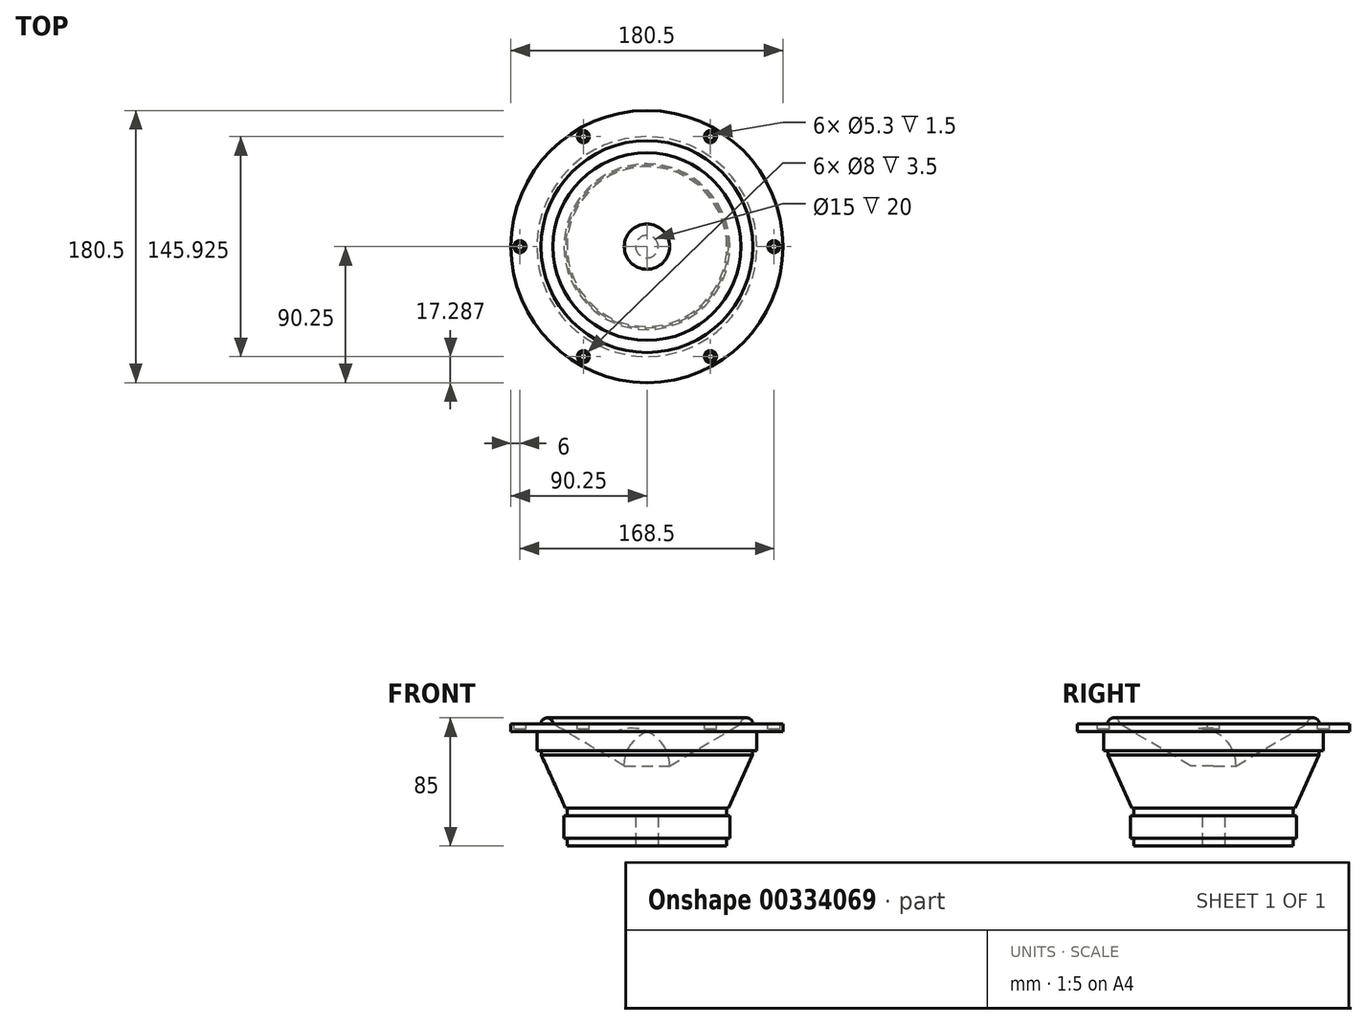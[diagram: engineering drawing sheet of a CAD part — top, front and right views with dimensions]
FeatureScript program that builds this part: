
annotation { "Feature Type Name" : "Feature", "Feature Type Description" : "" }
export const myFeature = defineFeature(function(context is Context, id is Id, definition is map)
    precondition{}
    {
        {
            var Q0;
            Q0=qCreatedBy(makeId("Right.planeOp"),FACE);
            var sketch = newSketch(context, id + "F0", { "sketchPlane" : qUnion([Q0])});
            skLineSegment(sketch, "E0", {"start": v(0, 0) * mm, "end": v(0, 35.91) * mm, "construction": true});
            skLineSegment(sketch, "E1", {"start": v(15, -22.91) * mm, "end": v(62.25, 5) * mm});
            skLineSegment(sketch, "E2", {"start": v(70.25, 5) * mm, "end": v(90.25, 5) * mm});
            skLineSegment(sketch, "E3", {"start": v(90.25, 5) * mm, "end": v(90.25, 0) * mm});
            skLineSegment(sketch, "E4", {"start": v(90.25, 0) * mm, "end": v(73, 0) * mm});
            skLineSegment(sketch, "E5", {"start": v(73, 0) * mm, "end": v(73, -12.7) * mm});
            skLineSegment(sketch, "E6", {"start": v(73, -12.7) * mm, "end": v(70, -12.7) * mm});
            skLineSegment(sketch, "E7", {"start": v(70, -12.7) * mm, "end": v(70, -15.7) * mm});
            skLineSegment(sketch, "E8", {"start": v(70, -15.7) * mm, "end": v(54, -51) * mm});
            skLineSegment(sketch, "E9", {"start": v(54, -51) * mm, "end": v(53, -51) * mm});
            skLineSegment(sketch, "E10", {"start": v(53, -51) * mm, "end": v(53, -56) * mm});
            skLineSegment(sketch, "E11", {"start": v(53, -56) * mm, "end": v(55, -56) * mm});
            skLineSegment(sketch, "E12", {"start": v(55, -56) * mm, "end": v(55, -71) * mm});
            skLineSegment(sketch, "E13", {"start": v(55, -71) * mm, "end": v(53, -71) * mm});
            skLineSegment(sketch, "E14", {"start": v(53, -71) * mm, "end": v(53, -76) * mm});
            skLineSegment(sketch, "E15", {"start": v(53, -76) * mm, "end": v(7.5, -76) * mm});
            skLineSegment(sketch, "E16", {"start": v(7.5, -76) * mm, "end": v(7.5, -56) * mm});
            skLineSegment(sketch, "E17", {"start": v(7.5, -56) * mm, "end": v(0, -56) * mm});
            skArc(sketch, "E18", {"start": v(70.25, 5) * mm, "mid": v(66.25, 9) * mm, "end": v(62.25, 5) * mm});
            skLineSegment(sketch, "E19", {"start": v(0, 0) * mm, "end": v(0, -56) * mm});
            skArc(sketch, "E20", {"start": v(15, -22.91) * mm, "mid": v(10.92, -9.22) * mm, "end": v(0, 0) * mm});
            skSolve(sketch);
        }
        {
            var Q0;
            Q0 = qSketchRegion(id + "F0", true);
            var Q1;
            Q1=sQuery(id+"F0.wireOp",EDGE,"E0");
            revolve(context, id + "F1", {"entities" : qUnion([Q0]), "axis" : qUnion([Q1]), "revolveType" : RevolveType.FULL});
        }
        {
            var Q0;
            Q0=makeQuery(id+"F1.opRevolve","SWEPT_FACE",FACE,{"disambiguationData":[OSD([sQuery(id+"F0.wireOp",EDGE,"E2")])]});
            var sketch = newSketch(context, id + "F2", { "sketchPlane" : qUnion([Q0])});
            skCircle(sketch, "E21.cCircle", {"center": v(0, 0) * mm, "radius": 84.25 * mm, "construction": true});
            skLineSegment(sketch, "E21.0", {"start": v(42.12, 72.96) * mm, "end": v(84.25, 0) * mm});
            skLineSegment(sketch, "E21.1", {"start": v(84.25, 0) * mm, "end": v(42.13, -72.96) * mm});
            skLineSegment(sketch, "E21.2", {"start": v(42.13, -72.96) * mm, "end": v(-42.12, -72.96) * mm});
            skLineSegment(sketch, "E21.3", {"start": v(-42.12, -72.96) * mm, "end": v(-84.25, 0) * mm});
            skLineSegment(sketch, "E21.4", {"start": v(-84.25, 0) * mm, "end": v(-42.13, 72.96) * mm});
            skLineSegment(sketch, "E21.5", {"start": v(-42.13, 72.96) * mm, "end": v(42.12, 72.96) * mm});
            skSolve(sketch);
        }
        {
            var Q0;
            Q0=sQuery(id+"F2.wireOp",VERTEX,"E21.0.start");
            var Q1;
            Q1=sQuery(id+"F2.wireOp",VERTEX,"E21.1.start");
            var Q2;
            Q2=sQuery(id+"F2.wireOp",VERTEX,"E21.2.start");
            var Q3;
            Q3=sQuery(id+"F2.wireOp",VERTEX,"E21.3.start");
            var Q4;
            Q4=sQuery(id+"F2.wireOp",VERTEX,"E21.4.start");
            var Q5;
            Q5=sQuery(id+"F2.wireOp",VERTEX,"E21.5.start");
            var Q6;
            Q6=makeQuery(id+"F1.opRevolve","SWEPT_BODY",BODY,{"disambiguationData":[OSD([sQuery(id+"F0.wireOp",EDGE,"E1"),sQuery(id+"F0.wireOp",EDGE,"E2"),sQuery(id+"F0.wireOp",EDGE,"E3"),sQuery(id+"F0.wireOp",EDGE,"E4"),sQuery(id+"F0.wireOp",EDGE,"E5"),sQuery(id+"F0.wireOp",EDGE,"E6"),sQuery(id+"F0.wireOp",EDGE,"E7"),sQuery(id+"F0.wireOp",EDGE,"E8"),sQuery(id+"F0.wireOp",EDGE,"E9"),sQuery(id+"F0.wireOp",EDGE,"E10"),sQuery(id+"F0.wireOp",EDGE,"E11"),sQuery(id+"F0.wireOp",EDGE,"E12"),sQuery(id+"F0.wireOp",EDGE,"E13"),sQuery(id+"F0.wireOp",EDGE,"E14"),sQuery(id+"F0.wireOp",EDGE,"E15"),sQuery(id+"F0.wireOp",EDGE,"E16"),sQuery(id+"F0.wireOp",EDGE,"E17"),sQuery(id+"F0.wireOp",EDGE,"E18"),sQuery(id+"F0.wireOp",EDGE,"6qJDFLsR-WWJ0-tgGE-hcnX-4yRczxiv6acq"),sQuery(id+"F0.wireOp",EDGE,"E19")])]});
            hole(context, id + "F3", {"style" : HoleStyle.C_BORE, "endStyle" : HoleEndStyle.THROUGH, "holeDiameter" : 5.3 * mm, "cBoreDiameter" : 8 * mm, "cBoreDepth" : 3.5 * mm, "tappedDepth" : 12 * mm, "tapClearance" : 3, "startFromSketch" : true, "locations" : qUnion([Q0, Q1, Q2, Q3, Q4, Q5]), "scope" : qUnion([Q6])});
        }
    });
